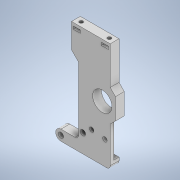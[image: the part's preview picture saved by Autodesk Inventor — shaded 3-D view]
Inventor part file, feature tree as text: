
AUTODESK INVENTOR PART (.ipt)
format: ipt  version: 2020.2 (Build 242310000, 310)  size: 260,096 bytes
history: native  units: mm
features: extrude x5, sketch x5, fillet x2, thread x2, mirror x1, projected_geometry x1
ambient origin geometry x8: Origin, YZ Plane, XZ Plane, XY Plane, X Axis, Y Axis, Z Axis, Center Point
bodies: Solid1 (feature_tree)
feature tree (16):
  extrude  "Extrusion1"  Depth=6.0mm
  fillet  "Fillet1"  Radius=28.0mm
  fillet  "Fillet2"  Radius=6.0mm
  extrude  "Extrusion2"  Depth=3.0mm
  extrude  "Extrusion3"  Depth=56.0mm
  thread  "Thread1"  [1 undecoded]
  thread  "Thread2"  [1 undecoded]
  mirror  "Mirror1"
  extrude  "Extrusion4"  Depth=12.5mm
  extrude  "Extrusion5"  Depth=2.0mm
  sketch  "Sketch1"  dims[d0=3.0mm d1=6.0mm d2=28.0mm d3=6.0mm]
  sketch  "Sketch2"  dims[d4=0.0mm d5=3.0mm]
  sketch  "Sketch3"  dims[d6=18.0mm d7=56.0mm d8=11.0mm d9=4.5mm]
  projected_geometry  "Projected Loop1"
  sketch  "Sketch5"  dims[d10=25.5mm d11=12.5mm]
  sketch  "Sketch6"  dims[d12=19.15mm d14=2.0mm d17=12.0mm d18=30.0mm d20=360.0deg d22=4.0mm d23=14.0mm d24=45.0deg d25=3.0mm d26=12.0mm d27=6.0mm d28=135.0deg d29=135.0deg d30=5.0mm d31=0.0mm d32=3.0mm d33=10.5mm d34=2.5mm d35=2.5mm d36=14.5mm d37=7.5mm d38=2.5mm d39=15.0mm d40=13.5mm d41=2.0mm d42=2.0mm d43=12.75mm d44=20.0mm d45=23.75mm d46=3.0mm d47=0.0mm d48=2.0mm d49=2.0mm d50=2.5mm d51=2.5mm d52=3.0mm d53=3.0mm d54=4.0mm d55=0.0mm d56=7.0mm d57=0.0mm d58=7.0mm d59=0.0mm d60=8.5mm d61=0.0mm d62=4.0mm d63=1.6mm d64=4.0mm d65=1.6mm d66=1.0mm d67=1.7mm d68=1.0mm d69=1.7mm d70=10.0mm d71=0.0mm d72=5.5mm d73=2.0mm d74=0.0mm]
note: 2 required parameter values undecoded (feature->parameter linkage not recoverable at this tier; creation-order binding heuristic only, values carry confidence <= 0.55)
